# Revit family: Lighting-Stradale-GEWISS-STREET[O3]-ARMATURE-LED_OTTICA_CICLOPEDONALE
name_source: partatom
category: Apparecchi per illuminazione
units: mm (PartAtom-declared; Revit-internal decimal feet)

## family parameters
Basato su piano di lavoro = No
Condiviso = No
Numero OmniClass = 23.80.70.00
Punto di calcolo locali = No
Quota connettore circolare = Usa diametro
Sempre verticale = Sì
Sorgente d'illuminazione = No
Taglio con vuoti quando caricato = No
Tipo di parte = Normale
Titolo OmniClass = Lighting

## types (1)
- Lighting-Stradale-GEWISS-STREET[O3]-ARMATURE-LED_OTTICA_CICLOPEDONALE
    Altezza da terra testa staffa = 822 mm
    Applicazione = Esterno
    Carico apparente = 68 VA
    Catalogo = LIGHTING
    Catalogo Serie = STREET [O3]
    Classe isolamento = II
    Codice EAN = 8011564804913
    Codice Electrocod = 244C
    Colore = Grafite/Alluminio
    Commenti sul wattaggio = 68W
    Corrente di pilotaggio LED = 700 mA
    Descrizione = STREET LED 2M 4000K 700mA CICLOPEDONALE
    Distanza minima dall'oggetto illuminato = 1M
    Flusso nominale (lm) = 8050
    Garanzia = 5 anni
    Grado di protezione = IP66
    IDF = 5129b26e-1484-42cf-ac1d-f4a2ab76f4d2
    IDT = fe79b716-81a6-4571-bc62-3b977ad29964
    Immagine tipo = GWS7001.jpg
    LED Life time (L80B10) = 100000H
    LED LifeTime (L80B20) = 50000H
    LED LifeTime (L90B20) = 50000H
    L_staffa = 120 mm  [stored 0.393701 ft]
    Lampada = LED
    Lampada: = LED
    Lumen output (lm) = 6330
    Materiale = Pressofusione di alluminio
    Modello = GWS7111
    N. moduli Chorus = 2 (2x16 LED)
    Numero di poli = 2
    Numero moduli = 2 (2x16 LED)
    Ottica = Ciclopedonale - ULOR: 0%
    Peso (kg) = 9,1
    Peso (kg): = 9,1
    Potenza di sistema = 68W
    Produttore = GEWISS S.p.A.
    Regolazione inclinazione = ±20° sbraccio - 0°÷20° testa palo
    Resistenza agli urti = IK08 CORPO - IK06 LENTI
    Rischio fotobiologico = RG1/RG2 @ 20cm
    Rischio fotobiologico: = RG1/RG2 @ 20cm
    SEO = Stradale
    Scheda Tecnica = https://www.gewiss.com
    Struttura = <Per categoria>
    Superficie massima esposta al vento = 0,26M2
    Temperatura di colore = 4000 K (CRI 70)
    Temperatura di colore: = 4000 K (CRI 70)
    Temperatura di funzionamento = -25 +25 °C
    Temperatura di utilizzo = -25 +35 °C
    Tensione = 220/240 V - 50/60 Hz - Stand alone e/o dimmerabile 1-10 V
    Tensione: = 220/240 V - 50/60 Hz
    Tipo alimentatore = Driver Led in corrente continua
    Tipologia = Stand alone
    URL = https://www.gewiss.com
    Versione file RFA = 20.11
    Vetro = GEWISS - Led - lm 650 / Temp_3000_K
    Voltaggio = 230 V

note: [stored X ft] marks values corroborated as IEEE doubles in the binary element streams (Revit-internal decimal feet)
